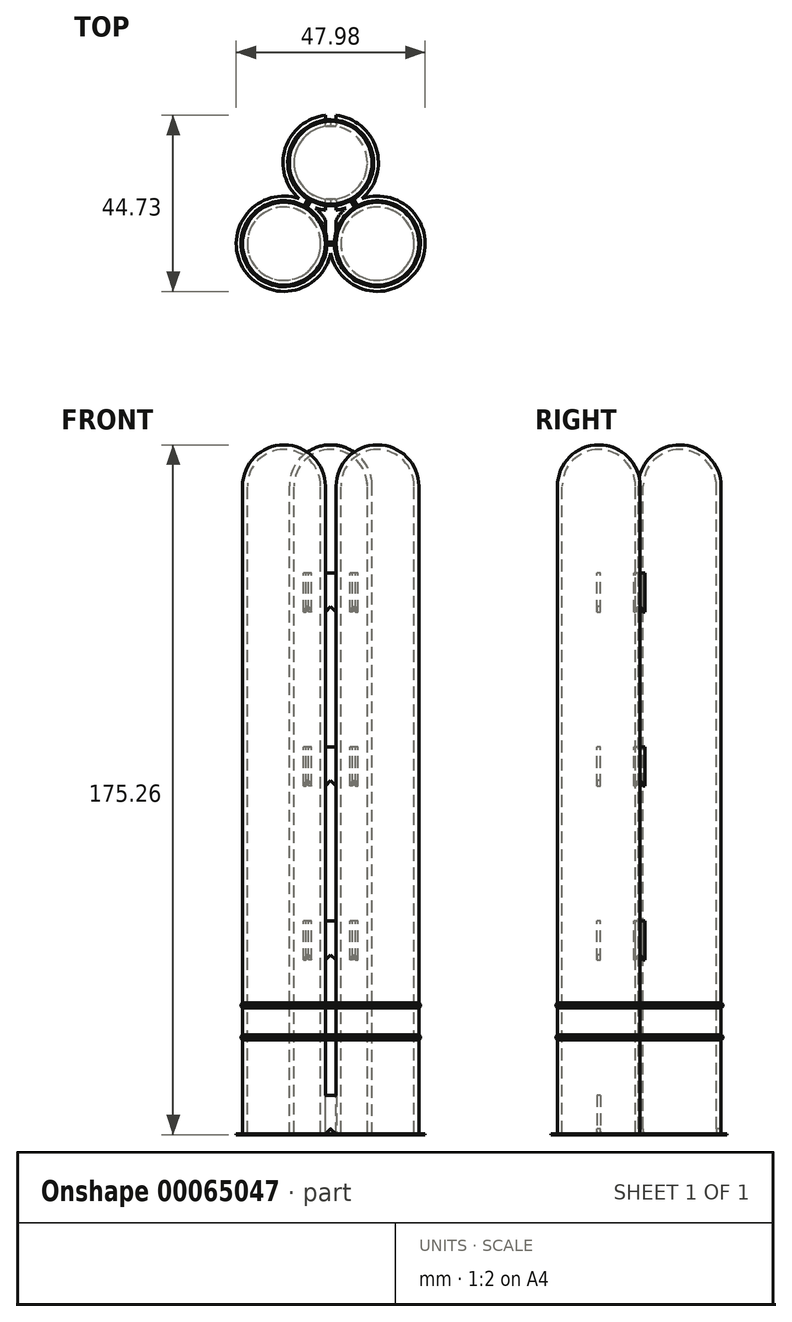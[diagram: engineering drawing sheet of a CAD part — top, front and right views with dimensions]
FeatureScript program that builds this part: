
annotation { "Feature Type Name" : "Feature", "Feature Type Description" : "" }
export const myFeature = defineFeature(function(context is Context, id is Id, definition is map)
    precondition{}
    {
        {
            var Q0;
            Q0=qCreatedBy(makeId("Front.planeOp"),FACE);
            var sketch = newSketch(context, id + "F0", { "sketchPlane" : qUnion([Q0])});
            skLineSegment(sketch, "E0", {"start": v(-9.31, 0) * mm, "end": v(-9.31, 164.75) * mm});
            skArc(sketch, "E1", {"start": v(-9.31, 164.75) * mm, "mid": v(-6.59, 171.33) * mm, "end": v(0, 174.06) * mm});
            skLineSegment(sketch, "E2", {"start": v(-10.51, 0) * mm, "end": v(-10.51, 164.75) * mm});
            skArc(sketch, "E3", {"start": v(-10.51, 164.75) * mm, "mid": v(-7.43, 172.18) * mm, "end": v(0, 175.26) * mm});
            skLineSegment(sketch, "E4", {"start": v(0, 175.26) * mm, "end": v(0, 174.06) * mm});
            skLineSegment(sketch, "E5", {"start": v(-10.51, 0) * mm, "end": v(-9.31, 0) * mm});
            skLineSegment(sketch, "E6", {"start": v(0, 174.06) * mm, "end": v(0, 0) * mm, "construction": true});
            skLineSegment(sketch, "E7.bottom", {"start": v(-10.51, 33.12) * mm, "end": v(-10.91, 33.12) * mm, "construction": true});
            skLineSegment(sketch, "E7.top", {"start": v(-10.51, 32.62) * mm, "end": v(-10.91, 32.62) * mm, "construction": true});
            skLineSegment(sketch, "E7.left", {"start": v(-10.51, 33.12) * mm, "end": v(-10.51, 32.62) * mm});
            skLineSegment(sketch, "E7.right", {"start": v(-10.91, 33.12) * mm, "end": v(-10.91, 32.62) * mm});
            skLineSegment(sketch, "E8.bottom", {"start": v(-10.51, 25) * mm, "end": v(-10.91, 25) * mm, "construction": true});
            skLineSegment(sketch, "E8.top", {"start": v(-10.51, 24.5) * mm, "end": v(-10.91, 24.5) * mm, "construction": true});
            skLineSegment(sketch, "E8.left", {"start": v(-10.51, 25) * mm, "end": v(-10.51, 24.5) * mm});
            skLineSegment(sketch, "E8.right", {"start": v(-10.91, 25) * mm, "end": v(-10.91, 24.5) * mm});
            skLineSegment(sketch, "E9", {"start": v(-10.91, 33.12) * mm, "end": v(-10.51, 33.52) * mm});
            skLineSegment(sketch, "E10", {"start": v(-10.91, 32.62) * mm, "end": v(-10.51, 32.22) * mm});
            skLineSegment(sketch, "E11", {"start": v(-10.91, 25) * mm, "end": v(-10.51, 25.4) * mm});
            skLineSegment(sketch, "E12", {"start": v(-10.91, 24.5) * mm, "end": v(-10.51, 24.1) * mm});
            skSolve(sketch);
        }
        {
            var Q0;
            {Q0=qUnion([makeQuery(id+"F0.imprint","IMPRINT",FACE,{"disambiguationData":[TD([[makeQuery(id+"F0.imprint","IMPRINT",EDGE,{"derivedFrom":sQuery(id+"F0.wireOp",EDGE,"E7.right")}),1.0]])]}),makeQuery(id+"F0.imprint","IMPRINT",FACE,{"disambiguationData":[TD([[makeQuery(id+"F0.imprint","IMPRINT",EDGE,{"derivedFrom":sQuery(id+"F0.wireOp",EDGE,"E8.right")}),1.0]])]}),makeQuery(id+"F0.imprint","IMPRINT",FACE,{"disambiguationData":[TD([[makeQuery(id+"F0.imprint","IMPRINT",EDGE,{"derivedFrom":sQuery(id+"F0.wireOp",EDGE,"E0")}),1.0]])]})]);}
            var Q1;
            Q1=sQuery(id+"F0.wireOp",EDGE,"E6");
            revolve(context, id + "F1", {"entities" : qUnion([Q0]), "axis" : qUnion([Q1]), "revolveType" : RevolveType.FULL});
        }
        {
            var Q0;
            Q0=makeQuery(id+"F1.opRevolve","SWEPT_EDGE",EDGE,{"disambiguationData":[OSD([sQuery(id+"F0.wireOp",EDGE,"E0"),sQuery(id+"F0.wireOp",EDGE,"E5")])]});
            fillet(context, id + "F2", {"entities" : qUnion([Q0]), "radius" : 0.5 * mm, "allowEdgeOverflow" : false});
        }
        {
            var Q0;
            Q0=qCreatedBy(makeId("Top.planeOp"),FACE);
            var sketch = newSketch(context, id + "F3", { "sketchPlane" : qUnion([Q0])});
            skCircle(sketch, "E13.0", {"center": v(0, 0) * mm, "radius": 10.51 * mm});
            skCircle(sketch, "E14.0", {"center": v(0, 0) * mm, "radius": 12.11 * mm});
            skLineSegment(sketch, "E15", {"start": v(0, 0) * mm, "end": v(0, 13.72) * mm, "construction": true});
            skSolve(sketch);
        }
        {
            var Q0;
            Q0 = qSketchRegion(id + "F3", true);
            extrude(context, id + "F4", {"entities" : qUnion([Q0]), "operationType" : NewBodyOperationType.ADD, "depth" : 0.15 * mm});
        }
        {
            var Q0;
            Q0=makeQuery(id+"F1.opRevolve","SWEPT_BODY",BODY,{"disambiguationData":[OSD([sQuery(id+"F0.wireOp",EDGE,"E0"),sQuery(id+"F0.wireOp",EDGE,"E1"),sQuery(id+"F0.wireOp",EDGE,"E2"),sQuery(id+"F0.wireOp",EDGE,"E3"),sQuery(id+"F0.wireOp",EDGE,"E4"),sQuery(id+"F0.wireOp",EDGE,"E5"),sQuery(id+"F0.wireOp",EDGE,"E7.right"),sQuery(id+"F0.wireOp",EDGE,"E8.right"),sQuery(id+"F0.wireOp",EDGE,"E9"),sQuery(id+"F0.wireOp",EDGE,"E10"),sQuery(id+"F0.wireOp",EDGE,"E11"),sQuery(id+"F0.wireOp",EDGE,"E12")])]});
            var Q1;
            Q1=sQuery(id+"F3.wireOp",EDGE,"E15");
            transform(context, id + "F5", {"entities" : qUnion([Q0]), "transformType" : TransformType.TRANSLATION_ENTITY, "oppositeDirectionEntity" : false, "transformLine" : qUnion([Q1]), "makeCopy" : false});
        }
        {
            var Q0;
            Q0=makeQuery(id+"F1.opRevolve","SWEPT_BODY",BODY,{"disambiguationData":[OSD([sQuery(id+"F0.wireOp",EDGE,"E0"),sQuery(id+"F0.wireOp",EDGE,"E1"),sQuery(id+"F0.wireOp",EDGE,"E2"),sQuery(id+"F0.wireOp",EDGE,"E3"),sQuery(id+"F0.wireOp",EDGE,"E4"),sQuery(id+"F0.wireOp",EDGE,"E5"),sQuery(id+"F0.wireOp",EDGE,"E7.right"),sQuery(id+"F0.wireOp",EDGE,"E8.right"),sQuery(id+"F0.wireOp",EDGE,"E9"),sQuery(id+"F0.wireOp",EDGE,"E10"),sQuery(id+"F0.wireOp",EDGE,"E11"),sQuery(id+"F0.wireOp",EDGE,"E12")])]});
            var Q1;
            Q1=sQuery(id+"F0.wireOp",EDGE,"E6");
            circularPattern(context, id + "F6", {"operationType" : NewBodyOperationType.ADD, "entities" : qUnion([Q0]), "axis" : qUnion([Q1]), "angle" : 360 * degree, "instanceCount" : 3, "equalSpace" : true});
        }
        {
            var Q0;
            Q0=qCreatedBy(makeId("Top.planeOp"),FACE);
            var sketch = newSketch(context, id + "F7", { "sketchPlane" : qUnion([Q0])});
            skCircle(sketch, "E16.0", {"center": v(-11.88, -6.86) * mm, "radius": 10.51 * mm, "construction": true});
            skCircle(sketch, "E17.0", {"center": v(11.88, -6.86) * mm, "radius": 10.51 * mm, "construction": true});
            skCircle(sketch, "E18.0", {"center": v(0, 13.72) * mm, "radius": 10.51 * mm, "construction": true});
            skLineSegment(sketch, "E19", {"start": v(-11.88, -6.86) * mm, "end": v(11.88, -6.86) * mm, "construction": true});
            skLineSegment(sketch, "E20.bottom", {"start": v(-1.46, -6.46) * mm, "end": v(1.46, -6.46) * mm});
            skLineSegment(sketch, "E20.top", {"start": v(-1.46, -7.26) * mm, "end": v(1.46, -7.26) * mm});
            skLineSegment(sketch, "E20.left", {"start": v(-1.46, -6.46) * mm, "end": v(-1.46, -7.26) * mm});
            skLineSegment(sketch, "E20.right", {"start": v(1.46, -6.46) * mm, "end": v(1.46, -7.26) * mm});
            skSolve(sketch);
        }
        {
            var Q0;
            Q0 = qSketchRegion(id + "F7", true);
            extrude(context, id + "F8", {"entities" : qUnion([Q0]), "depth" : 10 * mm});
        }
        {
            var Q0;
            Q0=makeQuery(id+"F8.opExtrude","SWEPT_FACE",FACE,{"disambiguationData":[OSD([sQuery(id+"F7.wireOp",EDGE,"E20.top")])]});
            var sketch = newSketch(context, id + "F9", { "sketchPlane" : qUnion([Q0])});
            skLineSegment(sketch, "E21.0.0", {"start": v(-1.46, 0) * mm, "end": v(1.46, 0) * mm, "construction": true});
            skLineSegment(sketch, "E21.0.1", {"start": v(1.46, 0) * mm, "end": v(1.46, 10) * mm, "construction": true});
            skLineSegment(sketch, "E21.0.2", {"start": v(1.46, 10) * mm, "end": v(-1.46, 10) * mm, "construction": true});
            skLineSegment(sketch, "E21.0.3", {"start": v(-1.46, 10) * mm, "end": v(-1.46, 0) * mm, "construction": true});
            skLineSegment(sketch, "E22", {"start": v(-1.46, 0) * mm, "end": v(0, 1.46) * mm});
            skLineSegment(sketch, "E23", {"start": v(0, 1.46) * mm, "end": v(1.46, 0) * mm});
            skLineSegment(sketch, "E24", {"start": v(-1.46, 0) * mm, "end": v(1.46, 0) * mm});
            skSolve(sketch);
        }
        {
            var Q0;
            Q0 = qSketchRegion(id + "F9", true);
            extrude(context, id + "F10", {"entities" : qUnion([Q0]), "operationType" : NewBodyOperationType.REMOVE, "endBound" : BoundingType.THROUGH_ALL, "oppositeDirection" : true, "depth" : 25 * mm});
        }
        {
            var Q0;
            Q0=makeQuery(id+"F8.opExtrude","SWEPT_BODY",BODY,{"disambiguationData":[OSD([sQuery(id+"F7.wireOp",EDGE,"E20.bottom"),sQuery(id+"F7.wireOp",EDGE,"E20.top"),sQuery(id+"F7.wireOp",EDGE,"E20.left"),sQuery(id+"F7.wireOp",EDGE,"E20.right")])]});
            transform(context, id + "F11", {"entities" : qUnion([Q0]), "transformType" : TransformType.TRANSLATION_3D, "dx" : 0 * mm, "dy" : 0 * mm, "dz" : (177 / 4) * mm, "makeCopy" : true});
        }
        {
            var Q0;
            Q0=makeQuery(id+"F11.opPattern","COPY",BODY,{"derivedFrom":makeQuery(id+"F8.opExtrude","SWEPT_BODY",BODY,{"disambiguationData":[OSD([sQuery(id+"F7.wireOp",EDGE,"E20.bottom"),sQuery(id+"F7.wireOp",EDGE,"E20.top"),sQuery(id+"F7.wireOp",EDGE,"E20.left"),sQuery(id+"F7.wireOp",EDGE,"E20.right")])]}),"instanceName":"1"});
            var Q1;
            Q1=sQuery(id+"F0.wireOp",EDGE,"E6");
            circularPattern(context, id + "F12", {"operationType" : NewBodyOperationType.ADD, "entities" : qUnion([Q0]), "axis" : qUnion([Q1]), "angle" : 360 * degree, "instanceCount" : 3, "equalSpace" : true});
        }
        {
            var Q0;
            Q0=makeQuery(id+"F8.opExtrude","SWEPT_BODY",BODY,{"disambiguationData":[OSD([sQuery(id+"F7.wireOp",EDGE,"E20.bottom"),sQuery(id+"F7.wireOp",EDGE,"E20.top"),sQuery(id+"F7.wireOp",EDGE,"E20.left"),sQuery(id+"F7.wireOp",EDGE,"E20.right")])]});
            transform(context, id + "F13", {"entities" : qUnion([Q0]), "transformType" : TransformType.TRANSLATION_3D, "dx" : 0 * mm, "dy" : 0 * mm, "dz" : (177 / 2) * mm, "makeCopy" : true});
        }
        {
            var Q0;
            Q0=makeQuery(id+"F13.opPattern","COPY",BODY,{"derivedFrom":makeQuery(id+"F8.opExtrude","SWEPT_BODY",BODY,{"disambiguationData":[OSD([sQuery(id+"F7.wireOp",EDGE,"E20.bottom"),sQuery(id+"F7.wireOp",EDGE,"E20.top"),sQuery(id+"F7.wireOp",EDGE,"E20.left"),sQuery(id+"F7.wireOp",EDGE,"E20.right")])]}),"instanceName":"1"});
            var Q1;
            Q1=sQuery(id+"F0.wireOp",EDGE,"E6");
            circularPattern(context, id + "F14", {"operationType" : NewBodyOperationType.ADD, "entities" : qUnion([Q0]), "axis" : qUnion([Q1]), "angle" : 360 * degree, "instanceCount" : 3, "equalSpace" : true});
        }
        {
            var Q0;
            Q0=makeQuery(id+"F8.opExtrude","SWEPT_BODY",BODY,{"disambiguationData":[OSD([sQuery(id+"F7.wireOp",EDGE,"E20.bottom"),sQuery(id+"F7.wireOp",EDGE,"E20.top"),sQuery(id+"F7.wireOp",EDGE,"E20.left"),sQuery(id+"F7.wireOp",EDGE,"E20.right")])]});
            transform(context, id + "F15", {"entities" : qUnion([Q0]), "transformType" : TransformType.TRANSLATION_3D, "dx" : 0 * mm, "dy" : 0 * mm, "dz" : (177 * 3 / 4) * mm, "makeCopy" : true});
        }
        {
            var Q0;
            Q0=makeQuery(id+"F15.opPattern","COPY",BODY,{"derivedFrom":makeQuery(id+"F8.opExtrude","SWEPT_BODY",BODY,{"disambiguationData":[OSD([sQuery(id+"F7.wireOp",EDGE,"E20.bottom"),sQuery(id+"F7.wireOp",EDGE,"E20.top"),sQuery(id+"F7.wireOp",EDGE,"E20.left"),sQuery(id+"F7.wireOp",EDGE,"E20.right")])]}),"instanceName":"1"});
            var Q1;
            Q1=sQuery(id+"F0.wireOp",EDGE,"E6");
            circularPattern(context, id + "F16", {"operationType" : NewBodyOperationType.ADD, "entities" : qUnion([Q0]), "axis" : qUnion([Q1]), "angle" : 360 * degree, "instanceCount" : 3, "equalSpace" : true});
        }
    });
